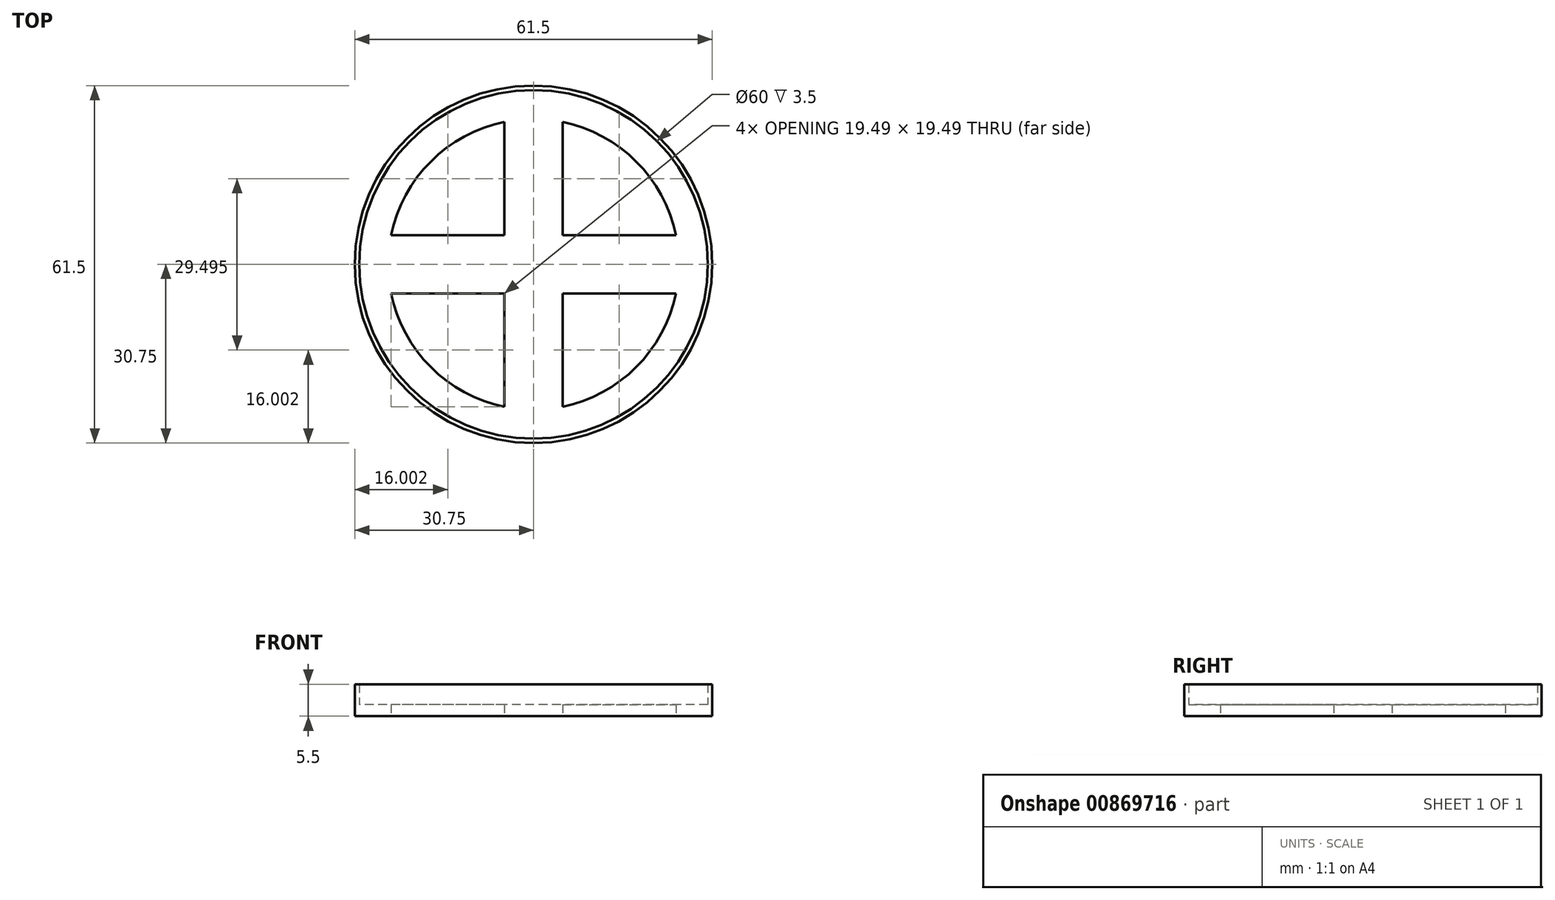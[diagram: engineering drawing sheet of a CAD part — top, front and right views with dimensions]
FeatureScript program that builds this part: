
annotation { "Feature Type Name" : "Feature", "Feature Type Description" : "" }
export const myFeature = defineFeature(function(context is Context, id is Id, definition is map)
    precondition{}
    {
        {
            var Q0;
            Q0=qCreatedBy(makeId("Top.planeOp"),FACE);
            var sketch = newSketch(context, id + "F0", { "sketchPlane" : qUnion([Q0])});
            skLineSegment(sketch, "E0", {"start": v(0, 0) * mm, "end": v(-30, 0) * mm});
            skLineSegment(sketch, "E1", {"start": v(0, 0) * mm, "end": v(0, 30) * mm});
            skLineSegment(sketch, "E2", {"start": v(0, 0) * mm, "end": v(30, 0) * mm});
            skLineSegment(sketch, "E3", {"start": v(0, 0) * mm, "end": v(0, -30) * mm});
            skArc(sketch, "E4", {"start": v(0, 30) * mm, "mid": v(21.21, 21.21) * mm, "end": v(30, 0) * mm});
            skArc(sketch, "E5", {"start": v(30, 0) * mm, "mid": v(21.21, -21.21) * mm, "end": v(0, -30) * mm});
            skArc(sketch, "E6", {"start": v(0, -30) * mm, "mid": v(-21.21, -21.21) * mm, "end": v(-30, 0) * mm});
            skArc(sketch, "E7", {"start": v(-30, 0) * mm, "mid": v(-21.21, 21.21) * mm, "end": v(0, 30) * mm});
            skLineSegment(sketch, "E8.0", {"start": v(5, 5) * mm, "end": v(5, 24.5) * mm});
            skLineSegment(sketch, "E8.1", {"start": v(5, 5) * mm, "end": v(24.5, 5) * mm});
            skArc(sketch, "E8.2", {"start": v(5, 24.5) * mm, "mid": v(17.68, 17.68) * mm, "end": v(24.5, 5) * mm});
            skLineSegment(sketch, "E9.0", {"start": v(5, -5) * mm, "end": v(24.5, -5) * mm});
            skLineSegment(sketch, "E9.1", {"start": v(5, -5) * mm, "end": v(5, -24.5) * mm});
            skArc(sketch, "E9.2", {"start": v(24.5, -5) * mm, "mid": v(17.68, -17.68) * mm, "end": v(5, -24.5) * mm});
            skLineSegment(sketch, "E10.0", {"start": v(-5, -5) * mm, "end": v(-5, -24.5) * mm});
            skLineSegment(sketch, "E10.1", {"start": v(-5, -5) * mm, "end": v(-24.5, -5) * mm});
            skArc(sketch, "E10.2", {"start": v(-5, -24.5) * mm, "mid": v(-17.68, -17.68) * mm, "end": v(-24.5, -5) * mm});
            skLineSegment(sketch, "E11.0", {"start": v(-5, 5) * mm, "end": v(-24.5, 5) * mm});
            skLineSegment(sketch, "E11.1", {"start": v(-5, 5) * mm, "end": v(-5, 24.5) * mm});
            skArc(sketch, "E11.2", {"start": v(-24.5, 5) * mm, "mid": v(-17.68, 17.68) * mm, "end": v(-5, 24.5) * mm});
            skCircle(sketch, "E12", {"center": v(0, 0) * mm, "radius": 30.75 * mm});
            skSolve(sketch);
        }
        {
            var Q0;
            Q0 = qSketchRegion(id + "F0", true);
            extrude(context, id + "F1", {"entities" : qUnion([Q0]), "depth" : 5.5 * mm, "offsetDistance" : 25 * mm});
        }
        {
            var Q0;
            Q0=makeQuery(id+"F0.imprint","IMPRINT",FACE,{"disambiguationData":[TD([[makeQuery(id+"F0.imprint","IMPRINT",EDGE,{"derivedFrom":sQuery(id+"F0.wireOp",EDGE,"E0")}),-1.0]])]});
            var Q1;
            Q1=makeQuery(id+"F0.imprint","IMPRINT",FACE,{"disambiguationData":[TD([[makeQuery(id+"F0.imprint","IMPRINT",EDGE,{"derivedFrom":sQuery(id+"F0.wireOp",EDGE,"E1")}),-1.0]])]});
            var Q2;
            Q2=makeQuery(id+"F0.imprint","IMPRINT",FACE,{"disambiguationData":[TD([[makeQuery(id+"F0.imprint","IMPRINT",EDGE,{"derivedFrom":sQuery(id+"F0.wireOp",EDGE,"E2")}),-1.0]])]});
            var Q3;
            Q3=makeQuery(id+"F0.imprint","IMPRINT",FACE,{"disambiguationData":[TD([[makeQuery(id+"F0.imprint","IMPRINT",EDGE,{"derivedFrom":sQuery(id+"F0.wireOp",EDGE,"E0")}),1.0]])]});
            extrude(context, id + "F2", {"entities" : qUnion([Q0, Q1, Q2, Q3]), "operationType" : NewBodyOperationType.ADD, "depth" : 2 * mm, "offsetDistance" : 25 * mm});
        }
    });
